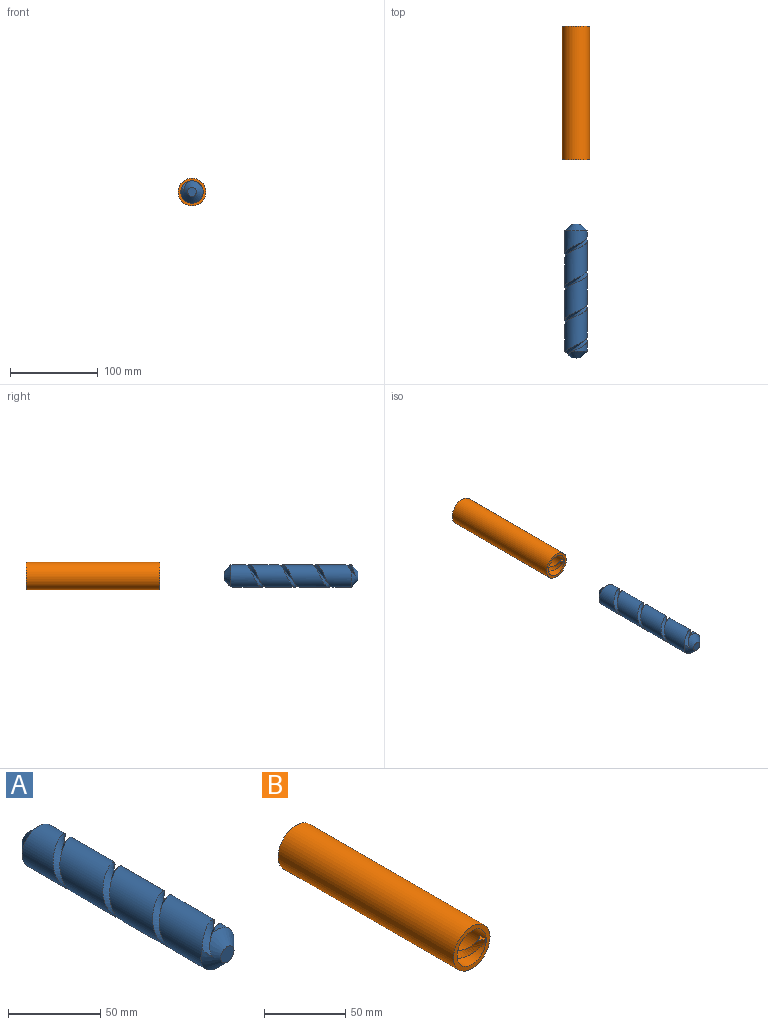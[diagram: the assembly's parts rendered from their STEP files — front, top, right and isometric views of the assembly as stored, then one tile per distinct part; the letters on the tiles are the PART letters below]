
ASSEMBLY  parts=2 mates=1
PART A: 7 faces, bbox 25.4x154.3x25.4 mm
  f0: cylinder r=12.7mm len=137.16mm, axis (0,1,0), area 9250.8mm2, adj f3,f4,f5,f6
  f1: plane 10.16x10.16mm, normal (0,-1,0), area 81.1mm2, adj f4
  f2: plane 10.16x10.16mm, normal (0,1,0), area 81.1mm2, adj f3
  f3: cone r=12.7mm half-angle=45deg, axis (0,-1,0), area 572.7mm2, adj f0,f2,f5,f6
  f4: cone r=5.08mm half-angle=45deg, axis (0,1,0), area 572.6mm2, adj f0,f1,f5,f6
  f5: bspline ~151.77x25.4mm, area 1394.7mm2, adj f0,f3,f4,f6
  f6: bspline ~151.77x25.4mm, area 1390.2mm2, adj f0,f3,f4,f5
PART B: 7 faces, bbox 32.1x157.8x32.1 mm
  f0: bspline ~154.94x25.4mm, area 1490.8mm2, adj f1,f4,f5,f6
  f1: bspline ~154.94x25.4mm, area 1459.9mm2, adj f0,f4,f5,f6
  f2: cylinder r=15.88mm len=152.4mm, axis (0,1,0), area 15201.2mm2, adj f3,f4
  f3: plane 31.75x31.75mm, normal (0,-1,0), area 285mm2, adj f2,f5
  f4: plane 32.09x32.09mm, normal (0,1,0), area 305.7mm2, adj f0,f1,f2,f5
  f5: cylinder r=12.7mm len=152.4mm, axis (0,-1,0), area 10708.2mm2, adj f0,f1,f3,f4,f6
  f6: plane 5.08x4.4mm, normal (0,0,1), area 11.2mm2, adj f0,f1,f5
PLACE A t=(-467.08,-268.32,-311.41)mm
PLACE B t=(-467.08,-42.26,-311.41)mm
MATE slider A.f0 <-> B.f5  axis (0,1,0) through (-467.08,-344.52,-311.41)mm
